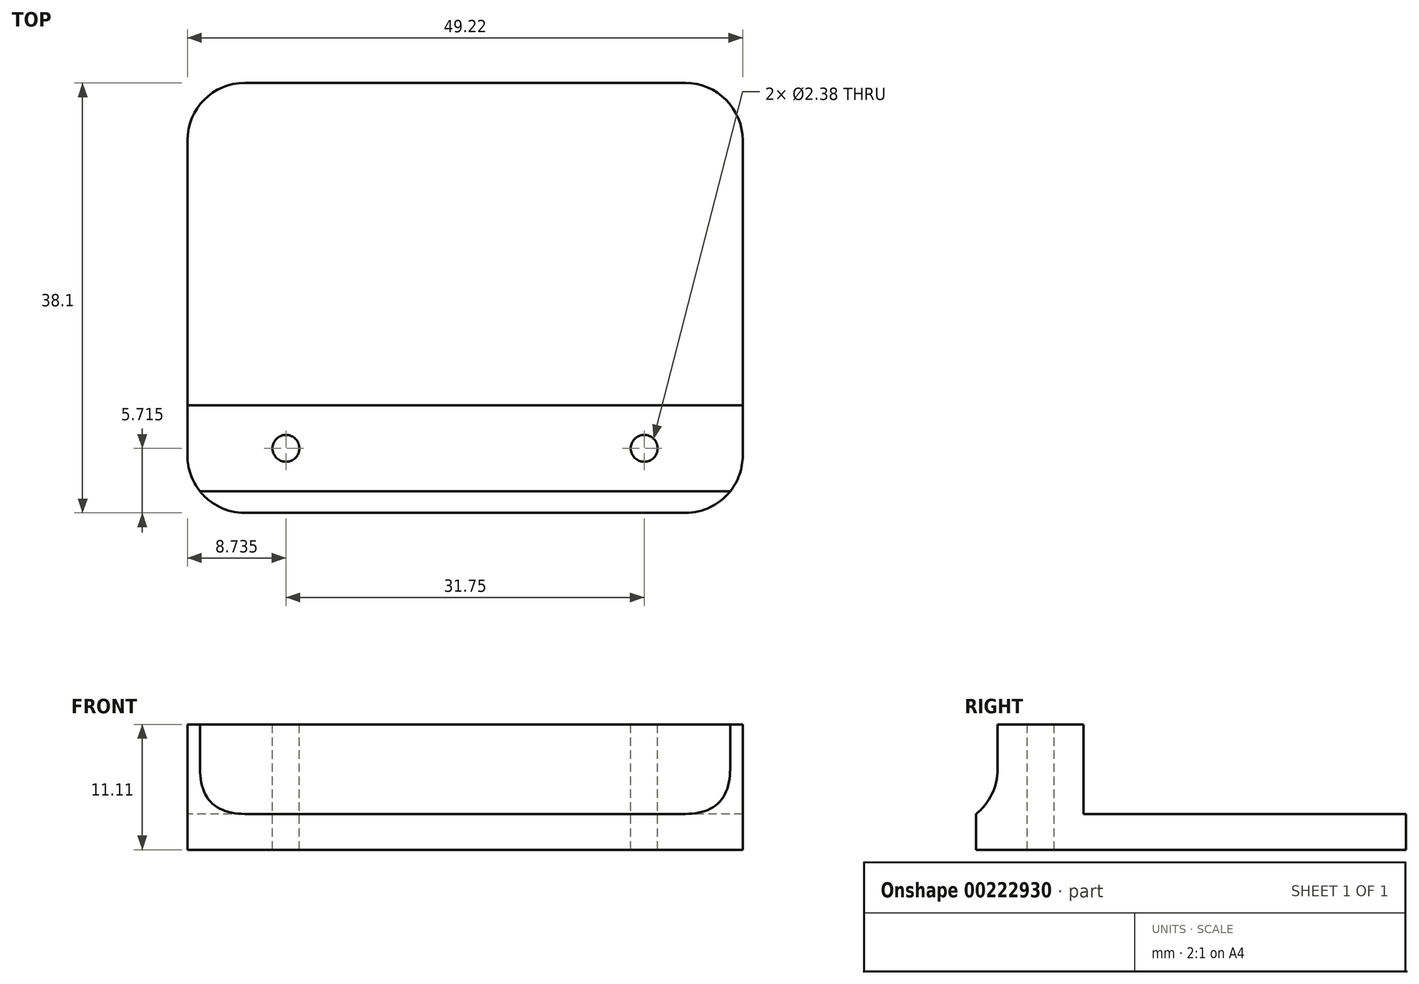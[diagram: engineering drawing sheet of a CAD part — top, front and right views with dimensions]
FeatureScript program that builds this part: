
annotation { "Feature Type Name" : "Feature", "Feature Type Description" : "" }
export const myFeature = defineFeature(function(context is Context, id is Id, definition is map)
    precondition{}
    {
        {
            var Q0;
            Q0=qCreatedBy(makeId("Top.planeOp"),FACE);
            var sketch = newSketch(context, id + "F0", { "sketchPlane" : qUnion([Q0])});
            skLineSegment(sketch, "E0.bottom", {"start": v(24.6, 19.05) * mm, "end": v(-24.6, 19.05) * mm});
            skLineSegment(sketch, "E0.top", {"start": v(24.6, -19.05) * mm, "end": v(-24.6, -19.05) * mm});
            skLineSegment(sketch, "E0.left", {"start": v(24.6, 19.05) * mm, "end": v(24.6, -19.05) * mm});
            skLineSegment(sketch, "E0.right", {"start": v(-24.6, 19.05) * mm, "end": v(-24.6, -19.05) * mm});
            skPoint(sketch, "E0.middle", {"position": v(0, 0) * mm});
            skSolve(sketch);
        }
        {
            var Q0;
            Q0 = qSketchRegion(id + "F0", true);
            extrude(context, id + "F1", {"entities" : qUnion([Q0]), "depth" : 3.17 * mm});
        }
        {
            var Q0;
            Q0=makeQuery(id+"F1.opExtrude","CAP_FACE",FACE,{"disambiguationData":[OSD([sQuery(id+"F0.wireOp",EDGE,"E0.bottom"),sQuery(id+"F0.wireOp",EDGE,"E0.top"),sQuery(id+"F0.wireOp",EDGE,"E0.left"),sQuery(id+"F0.wireOp",EDGE,"E0.right")])],"isStart":false});
            var sketch = newSketch(context, id + "F2", { "sketchPlane" : qUnion([Q0])});
            skLineSegment(sketch, "E1.bottom", {"start": v(24.6, -17.14) * mm, "end": v(-24.6, -17.15) * mm});
            skLineSegment(sketch, "E1.top", {"start": v(24.6, -9.52) * mm, "end": v(-24.6, -9.52) * mm});
            skLineSegment(sketch, "E1.left", {"start": v(24.6, -17.14) * mm, "end": v(24.6, -9.52) * mm});
            skLineSegment(sketch, "E1.right", {"start": v(-24.6, -17.15) * mm, "end": v(-24.6, -9.52) * mm});
            skPoint(sketch, "E1.middle", {"position": v(0, -13.33) * mm});
            skSolve(sketch);
        }
        {
            var Q0;
            Q0=makeQuery(id+"F2.imprint","IMPRINT",FACE,{"disambiguationData":[TD([[makeQuery(id+"F2.imprint","IMPRINT",EDGE,{"derivedFrom":sQuery(id+"F2.wireOp",EDGE,"E1.bottom")}),-1.0]])]});
            extrude(context, id + "F3", {"entities" : qUnion([Q0]), "operationType" : NewBodyOperationType.ADD, "depth" : 7.94 * mm});
        }
        {
            var Q0;
            Q0=makeQuery(id+"F3.opExtrude","CAP_FACE",FACE,{"disambiguationData":[OSD([sQuery(id+"F2.wireOp",EDGE,"E1.bottom"),sQuery(id+"F2.wireOp",EDGE,"E1.top"),sQuery(id+"F2.wireOp",EDGE,"E1.left"),sQuery(id+"F2.wireOp",EDGE,"E1.right")])],"isStart":false});
            var sketch = newSketch(context, id + "F4", { "sketchPlane" : qUnion([Q0])});
            skCircle(sketch, "E2", {"center": v(15.88, -13.33) * mm, "radius": 1.2 * mm});
            skCircle(sketch, "E3", {"center": v(-15.88, -13.34) * mm, "radius": 1.2 * mm});
            skSolve(sketch);
        }
        {
            var Q0;
            Q0=makeQuery(id+"F4.imprint","IMPRINT",FACE,{"disambiguationData":[TD([[makeQuery(id+"F4.imprint","IMPRINT",EDGE,{"derivedFrom":sQuery(id+"F4.wireOp",EDGE,"E3")}),1.0]])]});
            var Q1;
            Q1=makeQuery(id+"F4.imprint","IMPRINT",FACE,{"disambiguationData":[TD([[makeQuery(id+"F4.imprint","IMPRINT",EDGE,{"derivedFrom":sQuery(id+"F4.wireOp",EDGE,"E2")}),1.0]])]});
            extrude(context, id + "F5", {"entities" : qUnion([Q0, Q1]), "operationType" : NewBodyOperationType.REMOVE, "oppositeDirection" : true, "depth" : 25.4 * mm});
        }
        {
            var Q0;
            Q0=makeQuery(id+"F3.opExtrude","CAP_EDGE",EDGE,{"disambiguationData":[OSD([sQuery(id+"F2.wireOp",EDGE,"E1.bottom")])],"isStart":true});
            fillet(context, id + "F6", {"entities" : qUnion([Q0]), "radius" : 5.08 * mm, "tangentPropagation" : true, "allowEdgeOverflow" : false});
        }
        {
            var Q0;
            Q0=makeQuery(id+"F1.opExtrude","SWEPT_EDGE",EDGE,{"disambiguationData":[OSD([sQuery(id+"F0.wireOp",EDGE,"E0.top"),sQuery(id+"F0.wireOp",EDGE,"E0.right")])]});
            var Q1;
            Q1=makeQuery(id+"F1.opExtrude","SWEPT_EDGE",EDGE,{"disambiguationData":[OSD([sQuery(id+"F0.wireOp",EDGE,"E0.top"),sQuery(id+"F0.wireOp",EDGE,"E0.left")])]});
            var Q2;
            Q2=makeQuery(id+"F1.opExtrude","SWEPT_EDGE",EDGE,{"disambiguationData":[OSD([sQuery(id+"F0.wireOp",EDGE,"E0.bottom"),sQuery(id+"F0.wireOp",EDGE,"E0.left")])]});
            var Q3;
            Q3=makeQuery(id+"F1.opExtrude","SWEPT_EDGE",EDGE,{"disambiguationData":[OSD([sQuery(id+"F0.wireOp",EDGE,"E0.bottom"),sQuery(id+"F0.wireOp",EDGE,"E0.right")])]});
            fillet(context, id + "F7", {"entities" : qUnion([Q0, Q1, Q2, Q3]), "radius" : 5.08 * mm, "tangentPropagation" : true, "allowEdgeOverflow" : false});
        }
    });
